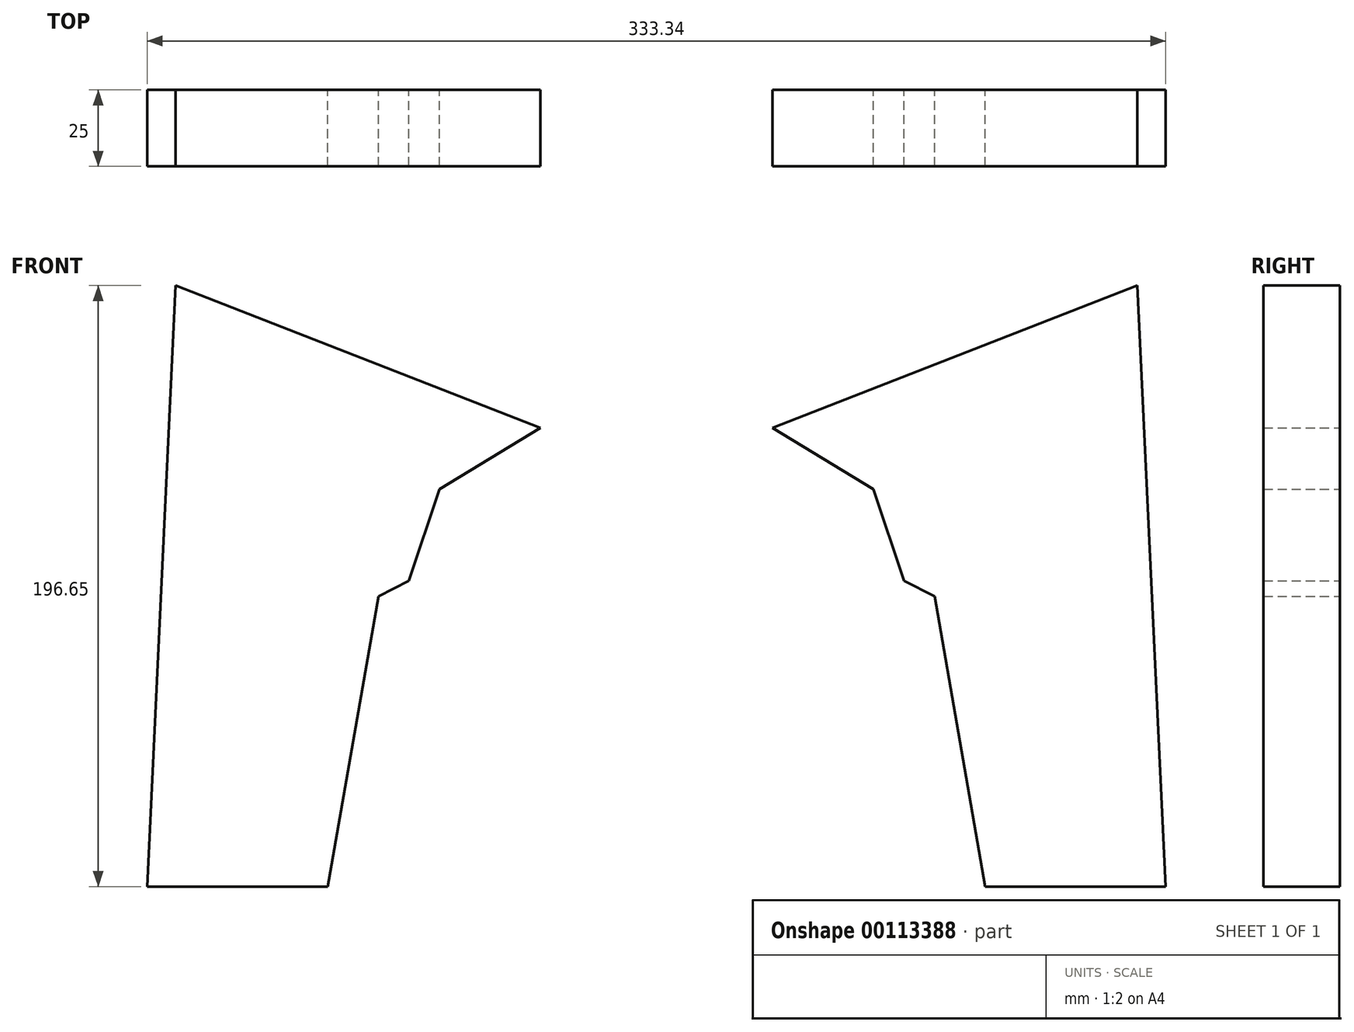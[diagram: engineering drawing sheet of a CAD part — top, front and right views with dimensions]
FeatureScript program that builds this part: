
annotation { "Feature Type Name" : "Feature", "Feature Type Description" : "" }
export const myFeature = defineFeature(function(context is Context, id is Id, definition is map)
    precondition{}
    {
        {
            var Q0;
            Q0=qCreatedBy(makeId("Front.planeOp"),FACE);
            var sketch = newSketch(context, id + "F0", { "sketchPlane" : qUnion([Q0])});
            skLineSegment(sketch, "E0", {"start": v(0, -597.53) * mm, "end": v(0, 62.47) * mm, "construction": true});
            skLineSegment(sketch, "E1", {"start": v(0, 62.47) * mm, "end": v(-38, 62.47) * mm, "construction": true});
            skLineSegment(sketch, "E2", {"start": v(0, 42.47) * mm, "end": v(-71, 42.47) * mm, "construction": true});
            skLineSegment(sketch, "E3", {"start": v(-38, 62.47) * mm, "end": v(-71, 42.47) * mm});
            skLineSegment(sketch, "E4", {"start": v(-71, 42.47) * mm, "end": v(-71, 12.47) * mm, "construction": true});
            skLineSegment(sketch, "E5", {"start": v(-71, 12.47) * mm, "end": v(-81, 12.47) * mm, "construction": true});
            skLineSegment(sketch, "E6", {"start": v(-71, 42.47) * mm, "end": v(-81, 12.47) * mm});
            skLineSegment(sketch, "E7", {"start": v(-81, 12.47) * mm, "end": v(-81, 7.47) * mm, "construction": true});
            skLineSegment(sketch, "E8", {"start": v(-81, 7.47) * mm, "end": v(-91, 7.47) * mm, "construction": true});
            skLineSegment(sketch, "E9", {"start": v(0, -87.53) * mm, "end": v(-107.58, -87.53) * mm, "construction": true});
            skLineSegment(sketch, "E10", {"start": v(-81, 12.47) * mm, "end": v(-91, 7.47) * mm});
            skLineSegment(sketch, "E11", {"start": v(-91, 7.47) * mm, "end": v(-107.58, -87.53) * mm});
            skLineSegment(sketch, "E12", {"start": v(-107.58, -87.53) * mm, "end": v(-166.67, -87.53) * mm});
            skLineSegment(sketch, "E13", {"start": v(-166.67, -87.53) * mm, "end": v(-157.39, 109.12) * mm});
            skLineSegment(sketch, "E14", {"start": v(-157.39, 109.12) * mm, "end": v(-38, 62.47) * mm});
            skLineSegment(sketch, "E15.MirrorCS", {"start": v(81, 12.47) * mm, "end": v(91, 7.47) * mm});
            skLineSegment(sketch, "E16.MirrorCS", {"start": v(81, 12.47) * mm, "end": v(81, 7.47) * mm, "construction": true});
            skLineSegment(sketch, "E17.MirrorCS", {"start": v(81, 7.47) * mm, "end": v(91, 7.47) * mm, "construction": true});
            skLineSegment(sketch, "E18.MirrorCS", {"start": v(71, 12.47) * mm, "end": v(81, 12.47) * mm, "construction": true});
            skLineSegment(sketch, "E19.MirrorCS", {"start": v(71, 42.47) * mm, "end": v(71, 12.47) * mm, "construction": true});
            skLineSegment(sketch, "E20.MirrorCS", {"start": v(0, 62.47) * mm, "end": v(38, 62.47) * mm, "construction": true});
            skLineSegment(sketch, "E21.MirrorCS", {"start": v(71, 42.47) * mm, "end": v(81, 12.47) * mm});
            skLineSegment(sketch, "E22.MirrorCS", {"start": v(166.67, -87.53) * mm, "end": v(157.39, 109.12) * mm});
            skLineSegment(sketch, "E23.MirrorCS", {"start": v(0, 42.47) * mm, "end": v(71, 42.47) * mm, "construction": true});
            skLineSegment(sketch, "E24.MirrorCS", {"start": v(0, -87.53) * mm, "end": v(107.58, -87.53) * mm, "construction": true});
            skLineSegment(sketch, "E25.MirrorCS", {"start": v(38, 62.47) * mm, "end": v(71, 42.47) * mm});
            skLineSegment(sketch, "E26.MirrorCS", {"start": v(91, 7.47) * mm, "end": v(107.58, -87.53) * mm});
            skLineSegment(sketch, "E27.MirrorCS", {"start": v(157.39, 109.12) * mm, "end": v(38, 62.47) * mm});
            skLineSegment(sketch, "E28.MirrorCS", {"start": v(107.58, -87.53) * mm, "end": v(166.67, -87.53) * mm});
            skSolve(sketch);
        }
        {
            var Q0;
            Q0=makeQuery(id+"F0.imprint","IMPRINT",FACE,{"disambiguationData":[TD([[makeQuery(id+"F0.imprint","IMPRINT",EDGE,{"derivedFrom":sQuery(id+"F0.wireOp",EDGE,"E15.MirrorCS")}),1.0]])]});
            var Q1;
            Q1=makeQuery(id+"F0.imprint","IMPRINT",FACE,{"disambiguationData":[TD([[makeQuery(id+"F0.imprint","IMPRINT",EDGE,{"derivedFrom":sQuery(id+"F0.wireOp",EDGE,"E3")}),-1.0]])]});
            extrude(context, id + "F1", {"entities" : qUnion([Q0, Q1]), "depth" : 25 * mm});
        }
    });
